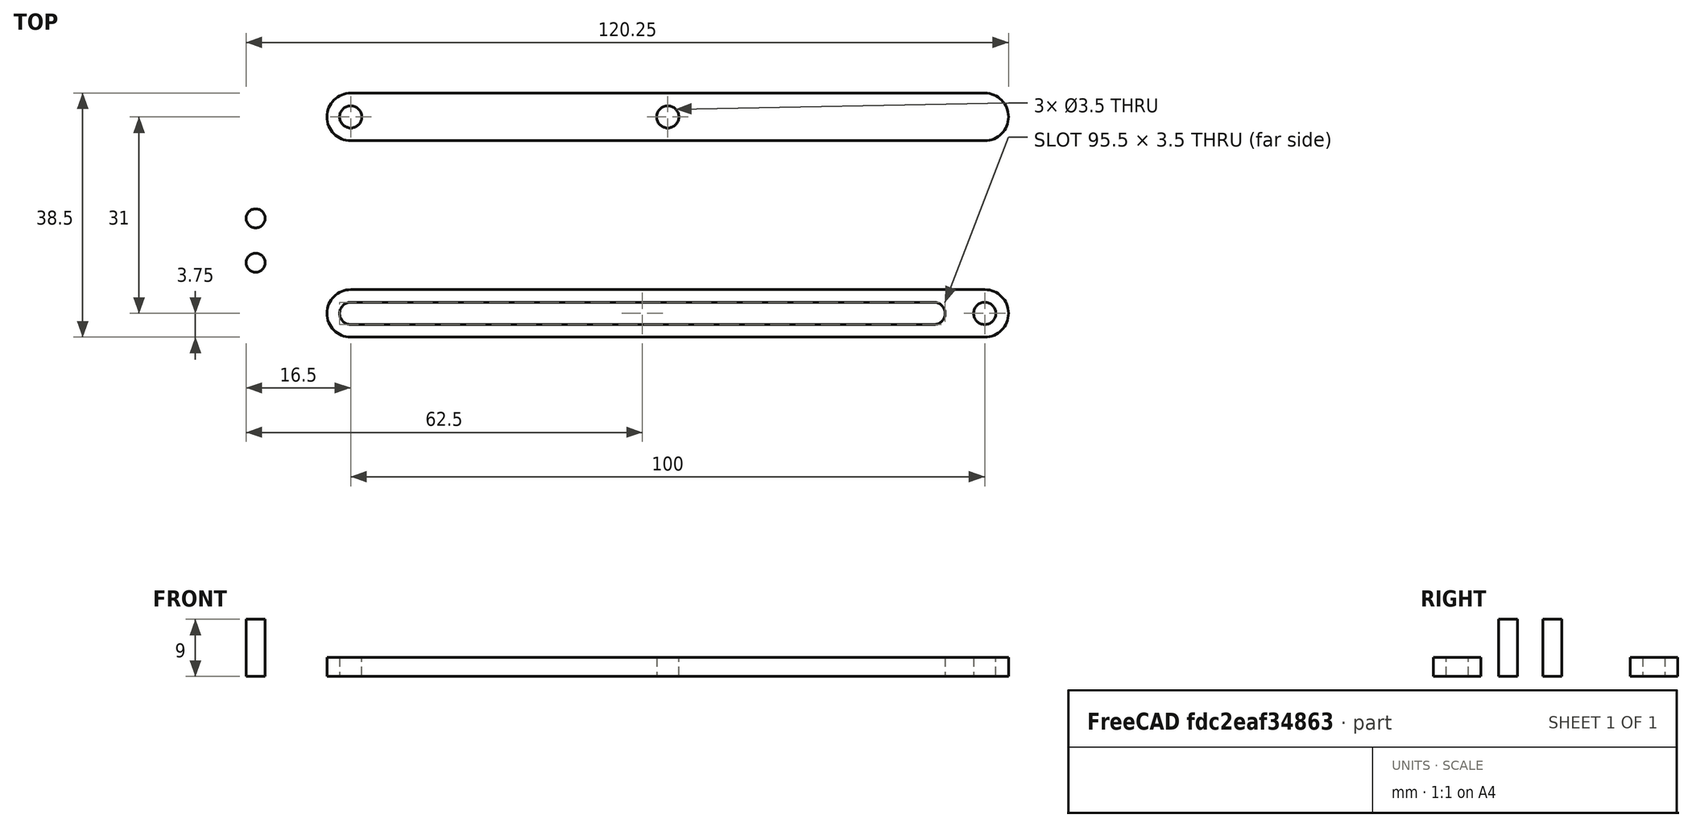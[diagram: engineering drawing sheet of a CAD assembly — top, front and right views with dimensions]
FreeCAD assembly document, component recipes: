
FREECAD ASSEMBLY — COMPONENT RECIPES ("sissor_lift")

This assembly document has 6 components, labeled P0..P5 below (a component is one placed body or linked part). 6 of them carry a construction recipe — the FreeCAD feature program that regenerates the part from scratch, quoted from this document or its linked companion documents; the rest are supplied as boundary geometry only. No exploded tour is included for this assembly.
COMPONENT P0 — recipe-attached ("base", modeled in this document).
Construction recipe (the document's own serialized feature program — sketch geometry with constraints, then the solid features built on it; lengths are millimeters unless a unit is written):

FEATURE [Sketcher::SketchObject] Sketch
  ArcFitTolerance = 1e-06
  AttachmentSupport = -> [XY_Plane]
  FullyConstrained = true
  MakeInternals = false
  MapMode = 5
  sketch-geometry (9):
    g0: ArcOfCircle CenterX=-50 CenterY=2e-16 CenterZ=0 NormalX=0 NormalY=0 NormalZ=1 AngleXU=0 Radius=3.75 StartAngle=1.5708 EndAngle=4.71239
    g1: ArcOfCircle CenterX=50 CenterY=-2e-16 CenterZ=0 NormalX=0 NormalY=0 NormalZ=1 AngleXU=0 Radius=3.75 StartAngle=4.71239 EndAngle=7.85398
    g2: LineSegment StartX=-50 StartY=3.75 StartZ=0 EndX=50 EndY=3.75 EndZ=0
    g3: LineSegment StartX=-50 StartY=-3.75 StartZ=0 EndX=50 EndY=-3.75 EndZ=0
    g4: ArcOfCircle CenterX=-50 CenterY=2e-16 CenterZ=0 NormalX=0 NormalY=0 NormalZ=1 AngleXU=0 Radius=1.75 StartAngle=1.5708 EndAngle=4.71239
    g5: ArcOfCircle CenterX=42 CenterY=3e-16 CenterZ=0 NormalX=0 NormalY=0 NormalZ=1 AngleXU=0 Radius=1.75 StartAngle=4.71239 EndAngle=7.85398
    g6: LineSegment StartX=-50 StartY=1.75 StartZ=0 EndX=42 EndY=1.75 EndZ=0
    g7: LineSegment StartX=-50 StartY=-1.75 StartZ=0 EndX=42 EndY=-1.75 EndZ=0
    g8: Circle CenterX=50 CenterY=-2e-16 CenterZ=0 NormalX=0 NormalY=0 NormalZ=1 AngleXU=0 Radius=1.75
  constraints (20):
    c: Tangent(g0,g2) = 1.5708
    c: Tangent(g0,g3) = -1.5708
    c: Tangent(g1,g2) = 1.5708
    c: Tangent(g1,g3) = -1.5708
    c: Equal(g0,g1)
    c: Horizontal(g3)
    c: Symmetric(g0,g1,g-1)
    c: DistanceX(g0,g1) = 100
    c: DistanceY(g0,g0) = 7.5
    c: Tangent(g4,g6) = 1.5708
    c: Tangent(g4,g7) = -1.5708
    c: Tangent(g5,g6) = 1.5708
    c: Tangent(g5,g7) = -1.5708
    c: Equal(g4,g5)
    c: Horizontal(g7)
    c: Distance(g4,g4) = 3.5
    c: Coincident(g8,g1)
    c: Diameter(g8) = 3.5
    c: DistanceX(g5,g1) = 8
    c: Coincident(g4,g0)
FEATURE [PartDesign::Pad] Pad
  Direction = (0,0,1)
  Length = 3
  Length2 = 10
  Profile = -> Sketch
  ReferenceAxis = -> Sketch [N_Axis]
  Refine = true
  Suppressed = false
  Type = 0
FEATURE [PartDesign::Body] Body  label="base"
  AllowCompound = false
  Group = -> [Sketch,Pad]
  Origin = -> Origin
  Tip = -> Pad
COMPONENT P1 — recipe-attached ("arm_1", modeled in this document).
Construction recipe (the document's own serialized feature program — sketch geometry with constraints, then the solid features built on it; lengths are millimeters unless a unit is written):

FEATURE [PartDesign::SubShapeBinder] Binder
  BindCopyOnChange = 0
  BindMode = 0
  ClaimChildren = false
  Context = -> Body001 [Binder.]
  Fuse = false
  MakeFace = true
  OffsetFill = false
  OffsetIntersection = false
  OffsetJoinType = 0
  OffsetOpenResult = false
  PartialLoad = false
  Refine = true
  Relative = true
  Support = -> [Body]
  _Version = 2
FEATURE [Sketcher::SketchObject] Sketch001
  ArcFitTolerance = 1e-06
  AttachmentSupport = -> [XY_Plane001]
  ExternalGeometry = -> [Binder]
  FullyConstrained = true
  MakeInternals = false
  MapMode = 5
  sketch-geometry (6):
    g0: ArcOfCircle CenterX=-50 CenterY=1e-16 CenterZ=0 NormalX=0 NormalY=0 NormalZ=1 AngleXU=0 Radius=3.75 StartAngle=1.5708 EndAngle=4.71239
    g1: ArcOfCircle CenterX=50 CenterY=-1e-16 CenterZ=0 NormalX=0 NormalY=0 NormalZ=1 AngleXU=0 Radius=3.75 StartAngle=4.71239 EndAngle=7.85398
    g2: LineSegment StartX=-50 StartY=3.75 StartZ=0 EndX=50 EndY=3.75 EndZ=0
    g3: LineSegment StartX=-50 StartY=-3.75 StartZ=0 EndX=50 EndY=-3.75 EndZ=0
    g4: Circle CenterX=-50 CenterY=1e-16 CenterZ=0 NormalX=0 NormalY=0 NormalZ=1 AngleXU=0 Radius=1.75
    g5: Circle CenterX=0 CenterY=0 CenterZ=0 NormalX=0 NormalY=0 NormalZ=1 AngleXU=0 Radius=1.75
  constraints (13):
    c: Tangent(g0,g2) = 1.5708
    c: Tangent(g0,g3) = -1.5708
    c: Tangent(g1,g2) = 1.5708
    c: Tangent(g1,g3) = -1.5708
    c: Equal(g0,g1)
    c: Horizontal(g2)
    c: Symmetric(g0,g1,g-1)
    c: Equal(g2,g-3)
    c: Equal(g1,g-4)
    c: Coincident(g4,g0)
    c: Equal(g4,g-5)
    c: Coincident(g5,g-1)
    c: Equal(g5,g-5)
FEATURE [PartDesign::Pad] Pad001
  Direction = (0,0,1)
  Length = 3
  Length2 = 10
  Profile = -> Sketch001
  ReferenceAxis = -> Sketch001 [N_Axis]
  Refine = true
  Suppressed = false
  Type = 0
FEATURE [PartDesign::Body] Body001  label="arm_1"
  AllowCompound = false
  Group = -> [Binder,Sketch001,Pad001]
  Origin = -> Origin001
  Placement = pos=(0,14,0) rot=(0,0,1;0rad)
  Tip = -> Pad001
COMPONENT P2 — recipe-attached ("arm_2", modeled in this document).
Construction recipe (the document's own serialized feature program — sketch geometry with constraints, then the solid features built on it; lengths are millimeters unless a unit is written):

FEATURE [PartDesign::FeatureBase] Clone
  BaseFeature = -> Body001
  Placement = pos=(0,14,0) rot=(0,0,1;0rad)
  Suppressed = false
FEATURE [PartDesign::Body] Body002  label="arm_2"
  AllowCompound = false
  Group = -> [Clone]
  Origin = -> Origin002
  Placement = pos=(0,17,0) rot=(0,0,1;0rad)
  Tip = -> Clone
COMPONENT P3 — recipe-attached ("pin_1", modeled in this document).
Construction recipe (the document's own serialized feature program — sketch geometry with constraints, then the solid features built on it; lengths are millimeters unless a unit is written):

FEATURE [Sketcher::SketchObject] Sketch002
  ArcFitTolerance = 1e-06
  AttachmentSupport = -> [XY_Plane003]
  FullyConstrained = true
  MakeInternals = false
  MapMode = 5
  sketch-geometry (1):
    g0: Circle CenterX=0 CenterY=0 CenterZ=0 NormalX=0 NormalY=0 NormalZ=1 AngleXU=0 Radius=1.5
  constraints (2):
    c: Coincident(g0,g-1)
    c: Diameter(g0) = 3
FEATURE [PartDesign::Pad] Pad002
  Direction = (0,0,1)
  Length = 9
  Length2 = 10
  Profile = -> Sketch002
  ReferenceAxis = -> Sketch002 [N_Axis]
  Refine = true
  Suppressed = false
  Type = 0
FEATURE [PartDesign::Body] Body003  label="pin_1"
  AllowCompound = false
  Group = -> [Sketch002,Pad002]
  Origin = -> Origin003
  Placement = pos=(-65,0,0) rot=(0,0,1;0rad)
  Tip = -> Pad002
COMPONENT P4 — recipe-attached ("pin_2", modeled in this document).
Construction recipe (the document's own serialized feature program — sketch geometry with constraints, then the solid features built on it; lengths are millimeters unless a unit is written):

FEATURE [PartDesign::FeatureBase] Clone001
  BaseFeature = -> Body003
  Placement = pos=(-65,0,0) rot=(0,0,1;0rad)
  Suppressed = false
FEATURE [PartDesign::Body] Body004  label="pin_2"
  AllowCompound = false
  Group = -> [Clone001]
  Origin = -> Origin004
  Placement = pos=(0,8,0) rot=(0,0,1;0rad)
  Tip = -> Clone001
COMPONENT P5 — recipe-attached ("pin_3", modeled in this document).
Construction recipe (the document's own serialized feature program — sketch geometry with constraints, then the solid features built on it; lengths are millimeters unless a unit is written):

FEATURE [PartDesign::FeatureBase] Clone002
  BaseFeature = -> Body003
  Placement = pos=(-65,0,0) rot=(0,0,1;0rad)
  Suppressed = false
FEATURE [PartDesign::Body] Body005  label="pin_3"
  AllowCompound = false
  Group = -> [Clone002]
  Origin = -> Origin005
  Placement = pos=(0,15,0) rot=(0,0,1;0rad)
  Tip = -> Clone002
PROVENANCE & LICENSES
A FreeCAD (.FCStd) document from a public repository crawl; recipes are the document's own serialized feature recipes (and, for linked parts, companion documents' recipes).
License: as declared in the source repository (recorded in the dataset sidecar).
